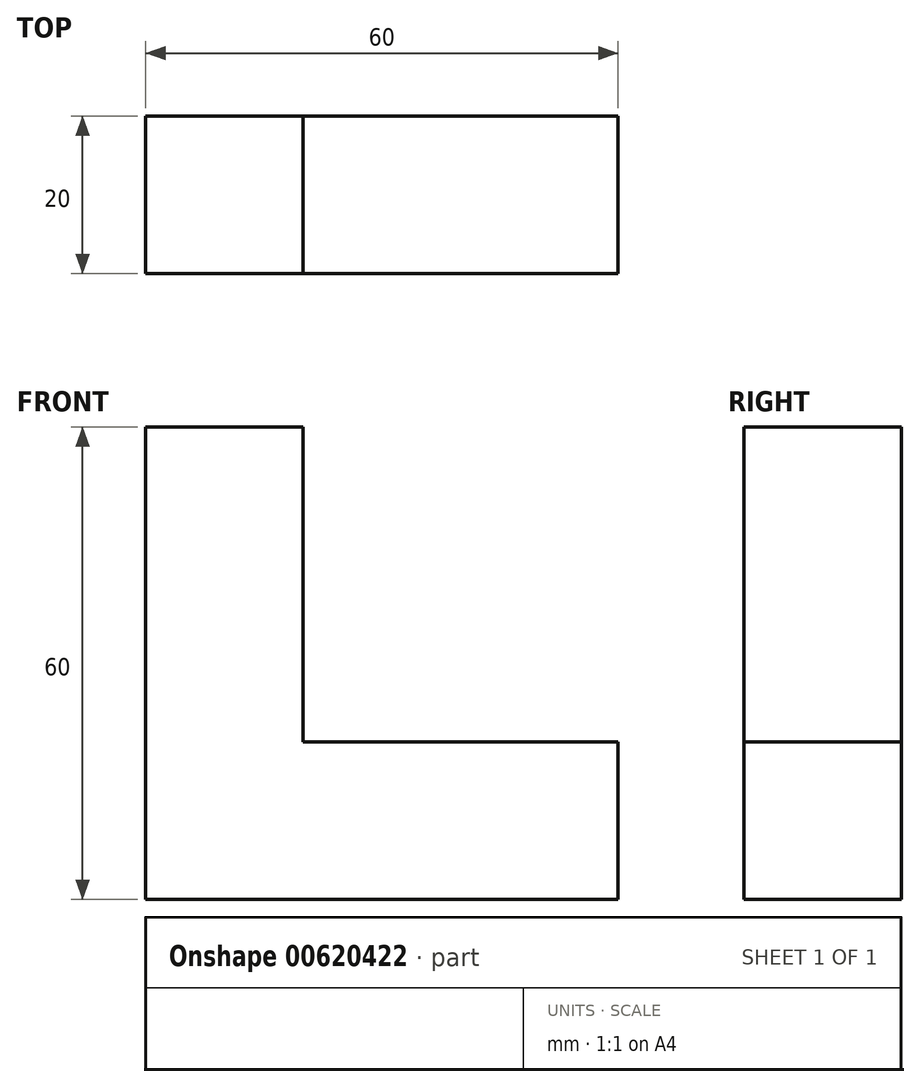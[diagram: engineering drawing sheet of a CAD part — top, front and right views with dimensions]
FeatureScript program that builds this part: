
annotation { "Feature Type Name" : "Feature", "Feature Type Description" : "" }
export const myFeature = defineFeature(function(context is Context, id is Id, definition is map)
    precondition{}
    {
        {
            var Q0;
            Q0=qCreatedBy(makeId("Front.planeOp"),FACE);
            var sketch = newSketch(context, id + "F0", { "sketchPlane" : qUnion([Q0])});
            skLineSegment(sketch, "E0", {"start": v(-55.53, 44.8) * mm, "end": v(-55.53, -15.2) * mm});
            skLineSegment(sketch, "E1", {"start": v(-55.53, -15.2) * mm, "end": v(4.47, -15.2) * mm});
            skLineSegment(sketch, "E2", {"start": v(4.47, -15.2) * mm, "end": v(4.47, 4.8) * mm});
            skLineSegment(sketch, "E3", {"start": v(4.47, 4.8) * mm, "end": v(-35.53, 4.8) * mm});
            skLineSegment(sketch, "E4", {"start": v(-35.53, 4.8) * mm, "end": v(-35.53, 44.8) * mm});
            skLineSegment(sketch, "E5", {"start": v(-35.53, 44.8) * mm, "end": v(-55.53, 44.8) * mm});
            skSolve(sketch);
        }
        {
            var Q0;
            Q0 = qSketchRegion(id + "F0", true);
            extrude(context, id + "F1", {"entities" : qUnion([Q0]), "depth" : 20 * mm, "offsetDistance" : 25 * mm});
        }
    });
